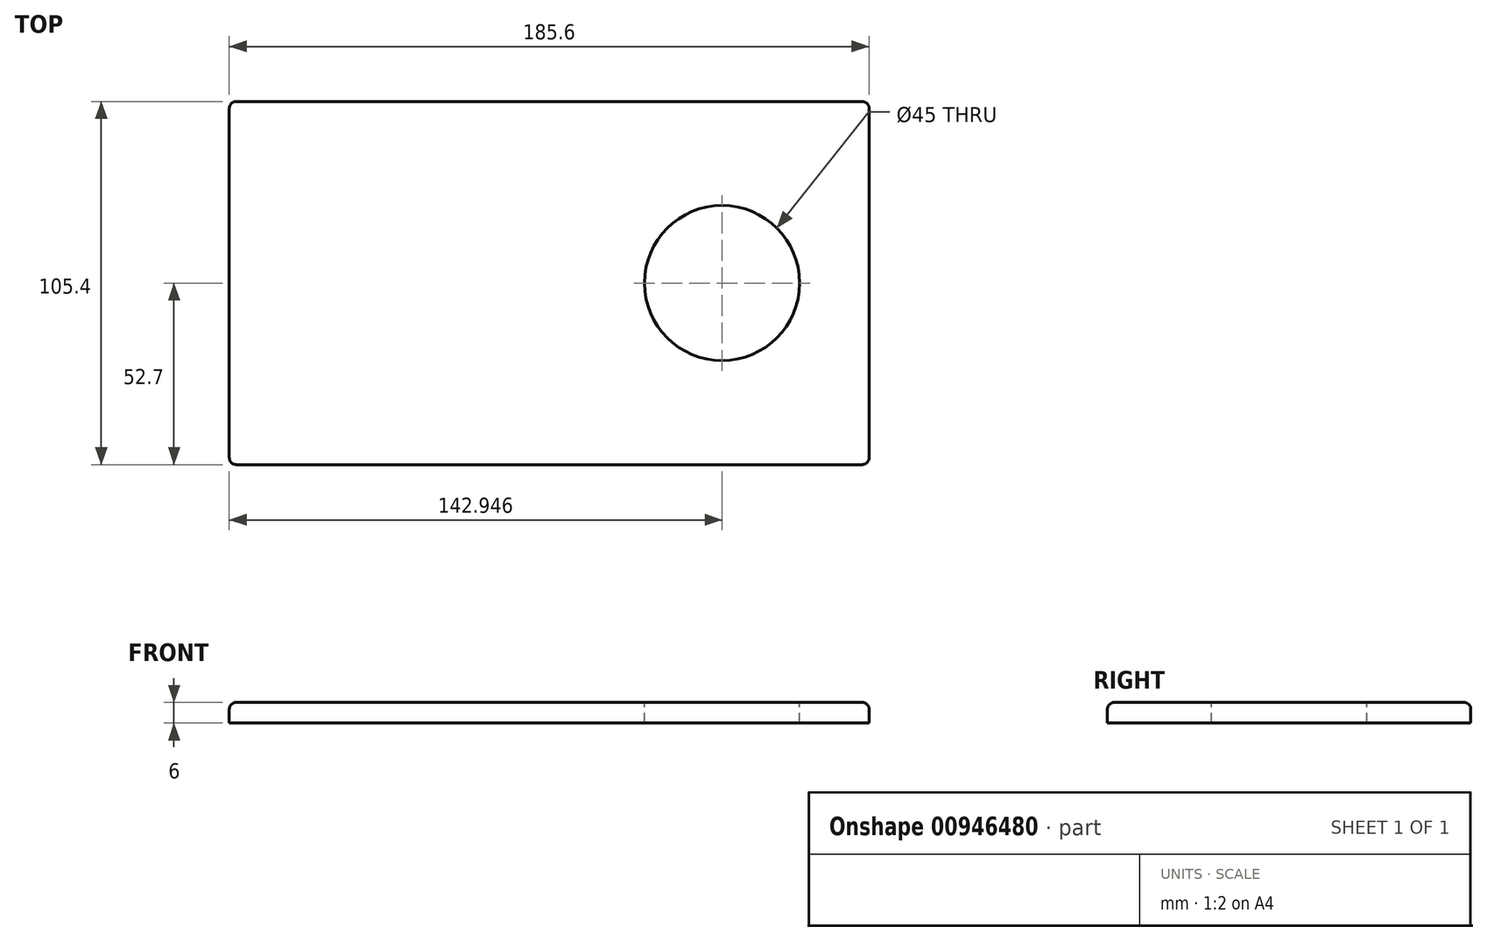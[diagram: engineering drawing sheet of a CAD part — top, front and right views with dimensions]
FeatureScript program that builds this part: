
annotation { "Feature Type Name" : "Feature", "Feature Type Description" : "" }
export const myFeature = defineFeature(function(context is Context, id is Id, definition is map)
    precondition{}
    {
        {
            var Q0;
            Q0=qCreatedBy(makeId("Top.planeOp"),FACE);
            var sketch = newSketch(context, id + "F0", { "sketchPlane" : qUnion([Q0])});
            skLineSegment(sketch, "E0.bottom", {"start": v(92.8, 52.7) * mm, "end": v(-92.8, 52.7) * mm});
            skLineSegment(sketch, "E0.top", {"start": v(92.8, -52.7) * mm, "end": v(-92.8, -52.7) * mm});
            skLineSegment(sketch, "E0.left", {"start": v(92.8, 52.7) * mm, "end": v(92.8, -52.7) * mm});
            skLineSegment(sketch, "E0.right", {"start": v(-92.8, 52.7) * mm, "end": v(-92.8, -52.7) * mm});
            skPoint(sketch, "E0.middle", {"position": v(0, 0) * mm});
            skSolve(sketch);
        }
        {
            var Q0;
            Q0=makeQuery(id+"F0.imprint","IMPRINT",FACE,{"disambiguationData":[TD([[makeQuery(id+"F0.imprint","IMPRINT",EDGE,{"derivedFrom":sQuery(id+"F0.wireOp",EDGE,"E0.bottom")}),1.0]])]});
            extrude(context, id + "F1", {"entities" : qUnion([Q0]), "depth" : 6 * mm, "offsetDistance" : 25 * mm});
        }
        {
            var Q0;
            Q0=makeQuery(id+"F1.opExtrude","CAP_FACE",FACE,{"disambiguationData":[OSD([sQuery(id+"F0.wireOp",EDGE,"E0.bottom"),sQuery(id+"F0.wireOp",EDGE,"E0.top"),sQuery(id+"F0.wireOp",EDGE,"E0.left"),sQuery(id+"F0.wireOp",EDGE,"E0.right")])],"isStart":false});
            var sketch = newSketch(context, id + "F2", { "sketchPlane" : qUnion([Q0])});
            skCircle(sketch, "E1", {"center": v(50.15, 0) * mm, "radius": 22.5 * mm});
            skSolve(sketch);
        }
        {
            var Q0;
            Q0=makeQuery(id+"F2.imprint","IMPRINT",FACE,{"disambiguationData":[TD([[makeQuery(id+"F2.imprint","IMPRINT",EDGE,{"derivedFrom":sQuery(id+"F2.wireOp",EDGE,"E1")}),1.0]])]});
            extrude(context, id + "F3", {"entities" : qUnion([Q0]), "operationType" : NewBodyOperationType.REMOVE, "oppositeDirection" : true, "depth" : 25 * mm, "offsetDistance" : 25 * mm});
        }
        {
            var Q0;
            Q0=makeQuery(id+"F1.opExtrude","CAP_EDGE",EDGE,{"disambiguationData":[OSD([sQuery(id+"F0.wireOp",EDGE,"E0.top")])],"isStart":false});
            var Q1;
            Q1=makeQuery(id+"F1.opExtrude","CAP_EDGE",EDGE,{"disambiguationData":[OSD([sQuery(id+"F0.wireOp",EDGE,"E0.left")])],"isStart":false});
            var Q2;
            Q2=makeQuery(id+"F1.opExtrude","CAP_EDGE",EDGE,{"disambiguationData":[OSD([sQuery(id+"F0.wireOp",EDGE,"E0.bottom")])],"isStart":false});
            var Q3;
            Q3=makeQuery(id+"F1.opExtrude","CAP_EDGE",EDGE,{"disambiguationData":[OSD([sQuery(id+"F0.wireOp",EDGE,"E0.right")])],"isStart":false});
            fillet(context, id + "F4", {"entities" : qUnion([Q0, Q1, Q2, Q3]), "radius" : 2 * mm, "tangentPropagation" : true, "allowEdgeOverflow" : false});
        }
        {
            var Q0;
            Q0=makeQuery(id+"F1.opExtrude","SWEPT_EDGE",EDGE,{"disambiguationData":[OSD([sQuery(id+"F0.wireOp",EDGE,"E0.top"),sQuery(id+"F0.wireOp",EDGE,"E0.left")])]});
            var Q1;
            Q1=makeQuery(id+"F1.opExtrude","SWEPT_EDGE",EDGE,{"disambiguationData":[OSD([sQuery(id+"F0.wireOp",EDGE,"E0.bottom"),sQuery(id+"F0.wireOp",EDGE,"E0.left")])]});
            var Q2;
            Q2=makeQuery(id+"F1.opExtrude","SWEPT_EDGE",EDGE,{"disambiguationData":[OSD([sQuery(id+"F0.wireOp",EDGE,"E0.bottom"),sQuery(id+"F0.wireOp",EDGE,"E0.right")])]});
            var Q3;
            Q3=makeQuery(id+"F1.opExtrude","SWEPT_EDGE",EDGE,{"disambiguationData":[OSD([sQuery(id+"F0.wireOp",EDGE,"E0.top"),sQuery(id+"F0.wireOp",EDGE,"E0.right")])]});
            fillet(context, id + "F5", {"entities" : qUnion([Q0, Q1, Q2, Q3]), "radius" : 2 * mm, "tangentPropagation" : true, "allowEdgeOverflow" : false});
        }
    });
